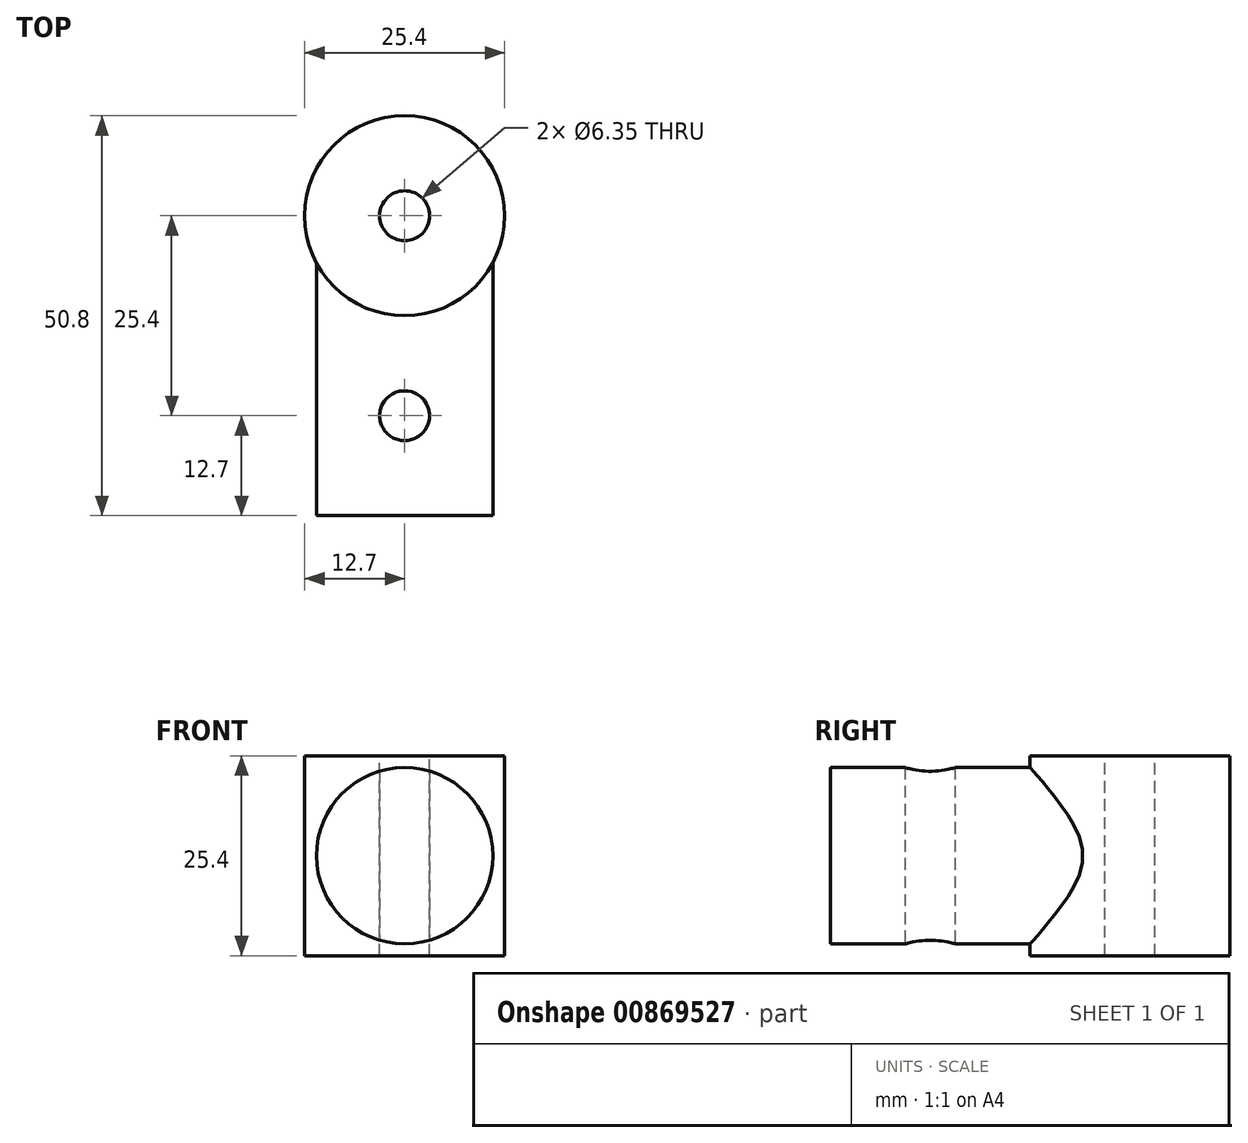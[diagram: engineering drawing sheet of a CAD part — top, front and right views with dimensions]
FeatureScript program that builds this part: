
annotation { "Feature Type Name" : "Feature", "Feature Type Description" : "" }
export const myFeature = defineFeature(function(context is Context, id is Id, definition is map)
    precondition{}
    {
        {
            var Q0;
            Q0=qCreatedBy(makeId("Top.planeOp"),FACE);
            var sketch = newSketch(context, id + "F0", { "sketchPlane" : qUnion([Q0])});
            skCircle(sketch, "E0", {"center": v(0, 0) * mm, "radius": 12.7 * mm});
            skSolve(sketch);
        }
        {
            var Q0;
            Q0 = qSketchRegion(id + "F0", true);
            extrude(context, id + "F1", {"entities" : qUnion([Q0]), "depth" : 25.4 * mm, "offsetDistance" : 25.4 * mm});
        }
        {
            var Q0;
            Q0=qCreatedBy(makeId("Front.planeOp"),FACE);
            var sketch = newSketch(context, id + "F2", { "sketchPlane" : qUnion([Q0])});
            skCircle(sketch, "E1", {"center": v(0, 12.7) * mm, "radius": 12.7 * mm, "construction": true});
            skCircle(sketch, "E2.0", {"center": v(0, 12.7) * mm, "radius": 11.2 * mm});
            skSolve(sketch);
        }
        {
            var Q0;
            Q0 = qSketchRegion(id + "F2", true);
            extrude(context, id + "F3", {"entities" : qUnion([Q0]), "operationType" : NewBodyOperationType.ADD, "depth" : 38.1 * mm, "offsetDistance" : 25.4 * mm});
        }
        {
            var Q0;
            Q0=qCreatedBy(makeId("Top.planeOp"),FACE);
            var sketch = newSketch(context, id + "F4", { "sketchPlane" : qUnion([Q0])});
            skCircle(sketch, "E3", {"center": v(0, 0) * mm, "radius": 3.18 * mm});
            skSolve(sketch);
        }
        {
            var Q0;
            Q0 = qSketchRegion(id + "F4", true);
            extrude(context, id + "F5", {"entities" : qUnion([Q0]), "operationType" : NewBodyOperationType.REMOVE, "oppositeDirection" : true, "depth" : 25.4 * mm, "offsetDistance" : 25.4 * mm, "hasSecondDirection" : true, "secondDirectionOppositeDirection" : false, "secondDirectionDepth" : 25.4 * mm});
        }
        {
            var Q0;
            Q0=makeQuery(id+"F1.opExtrude","CAP_FACE",FACE,{"disambiguationData":[OSD([sQuery(id+"F0.wireOp",EDGE,"E0")])],"isStart":false});
            cPlane(context, id + "F6", {"entities" : qUnion([Q0]), "cplaneType" : CPlaneType.OFFSET, "offset" : 12.7 * mm, "oppositeDirection" : true, "width" : 152.4 * mm, "height" : 152.4 * mm});
        }
        {
            var Q0;
            Q0=qCreatedBy(id+"F6.planeOp",FACE);
            var sketch = newSketch(context, id + "F7", { "sketchPlane" : qUnion([Q0])});
            skLineSegment(sketch, "E4", {"start": v(0, 0) * mm, "end": v(0, -38.1) * mm, "construction": true});
            skCircle(sketch, "E5", {"center": v(0, -25.4) * mm, "radius": 3.18 * mm});
            skSolve(sketch);
        }
        {
            var Q0;
            Q0 = qSketchRegion(id + "F7", true);
            extrude(context, id + "F8", {"entities" : qUnion([Q0]), "operationType" : NewBodyOperationType.REMOVE, "endBound" : BoundingType.SYMMETRIC, "depth" : 25.4 * mm, "offsetDistance" : 25.4 * mm});
        }
    });
